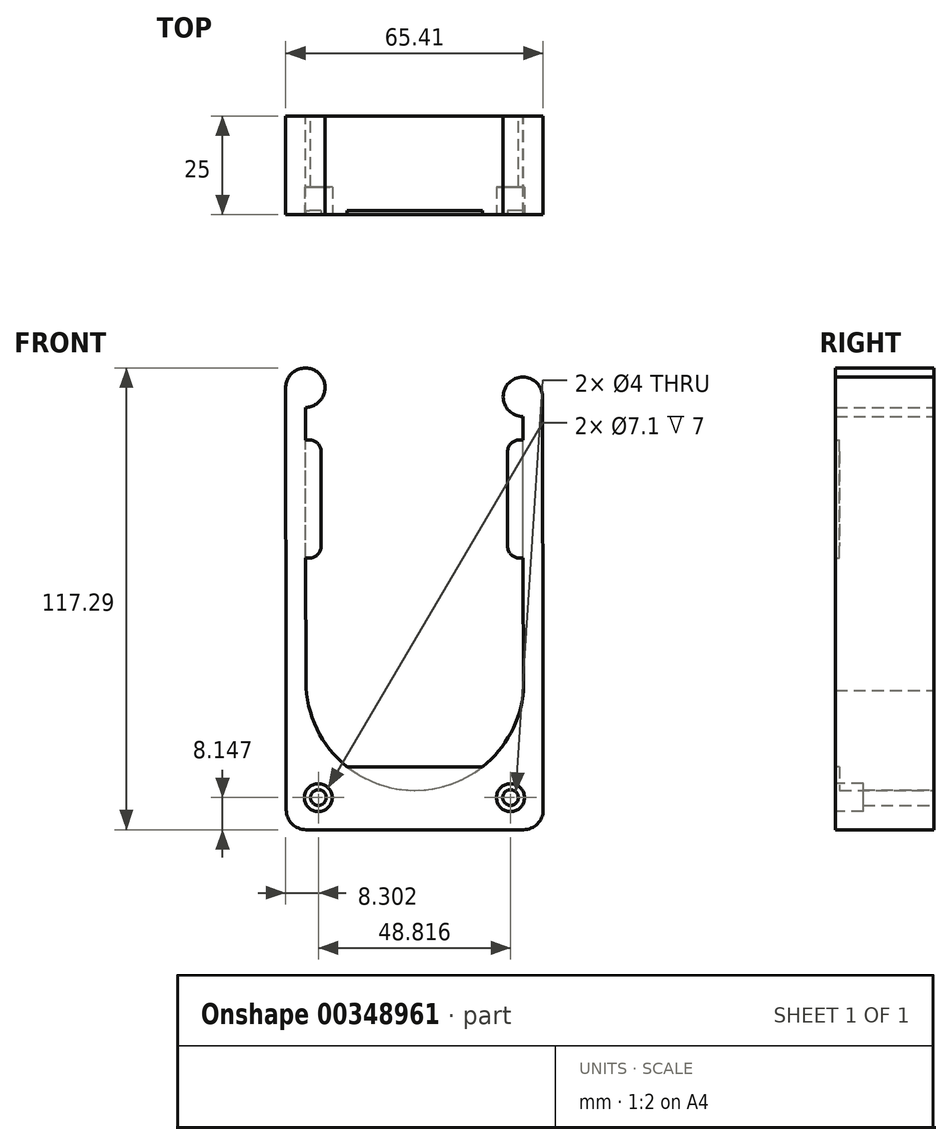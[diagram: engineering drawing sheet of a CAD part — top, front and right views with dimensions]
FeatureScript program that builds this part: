
annotation { "Feature Type Name" : "Feature", "Feature Type Description" : "" }
export const myFeature = defineFeature(function(context is Context, id is Id, definition is map)
    precondition{}
    {
        {
            var Q0;
            Q0=qCreatedBy(makeId("Front.planeOp"),FACE);
            var sketch = newSketch(context, id + "F0", { "sketchPlane" : qUnion([Q0])});
            skLineSegment(sketch, "E0.left", {"start": v(27.7, -35.98) * mm, "end": v(27.56, 33.69) * mm});
            skLineSegment(sketch, "E0.right", {"start": v(-27.56, -33.69) * mm, "end": v(-27.7, 35.98) * mm});
            skPoint(sketch, "E0.middle", {"position": v(0, 0) * mm});
            skArc(sketch, "E1", {"start": v(-27.56, -33.69) * mm, "mid": v(-1.03, -61.3) * mm, "end": v(27.7, -35.98) * mm});
            skLineSegment(sketch, "E2.1", {"start": v(32.7, -35.94) * mm, "end": v(32.55, 38.7) * mm});
            skLineSegment(sketch, "E2.3", {"start": v(-32.56, -36.07) * mm, "end": v(-32.71, 40.93) * mm});
            skArc(sketch, "E3", {"start": v(32.55, 38.7) * mm, "mid": v(24.01, 42.21) * mm, "end": v(27.56, 33.69) * mm});
            skArc(sketch, "E4", {"start": v(-27.7, 35.98) * mm, "mid": v(-24.2, 44.54) * mm, "end": v(-32.71, 40.93) * mm});
            skLineSegment(sketch, "E5", {"start": v(-32.56, -36.07) * mm, "end": v(-32.56, -66.31) * mm});
            skLineSegment(sketch, "E6", {"start": v(-27.56, -71.31) * mm, "end": v(27.7, -71.31) * mm});
            skLineSegment(sketch, "E7", {"start": v(32.7, -66.31) * mm, "end": v(32.7, -35.94) * mm});
            skLineSegment(sketch, "E8", {"start": v(0, 0) * mm, "end": v(0, -61.31) * mm, "construction": true});
            skPoint(sketch, "E9.visualSharp", {"position": v(-32.56, -71.31) * mm});
            skArc(sketch, "E9.filletArc", {"start": v(-32.56, -66.31) * mm, "mid": v(-31.1, -69.85) * mm, "end": v(-27.56, -71.31) * mm});
            skPoint(sketch, "E10.visualSharp", {"position": v(32.7, -71.31) * mm});
            skArc(sketch, "E10.filletArc", {"start": v(27.7, -71.31) * mm, "mid": v(31.24, -69.85) * mm, "end": v(32.7, -66.31) * mm});
            skCircle(sketch, "E11", {"center": v(-24.4, -63.16) * mm, "radius": 2 * mm});
            skLineSegment(sketch, "E12", {"start": v(-16.8, -55.55) * mm, "end": v(-31.1, -69.85) * mm, "construction": true});
            skCircle(sketch, "E13.MirrorC", {"center": v(24.4, -63.16) * mm, "radius": 2 * mm});
            skSolve(sketch);
        }
        {
            var Q0;
            Q0 = qSketchRegion(id + "F0", true);
            extrude(context, id + "F1", {"entities" : qUnion([Q0]), "depth" : 25 * mm});
        }
        {
            var Q0;
            Q0=makeQuery(id+"F1.opExtrude","CAP_FACE",FACE,{"disambiguationData":[OSD([sQuery(id+"F0.wireOp",EDGE,"E0.left"),sQuery(id+"F0.wireOp",EDGE,"E0.right"),sQuery(id+"F0.wireOp",EDGE,"E1"),sQuery(id+"F0.wireOp",EDGE,"E2.1"),sQuery(id+"F0.wireOp",EDGE,"E2.3"),sQuery(id+"F0.wireOp",EDGE,"E3"),sQuery(id+"F0.wireOp",EDGE,"E4"),sQuery(id+"F0.wireOp",EDGE,"E5"),sQuery(id+"F0.wireOp",EDGE,"E6"),sQuery(id+"F0.wireOp",EDGE,"E7"),sQuery(id+"F0.wireOp",EDGE,"E9.filletArc"),sQuery(id+"F0.wireOp",EDGE,"E10.filletArc"),sQuery(id+"F0.wireOp",EDGE,"E11"),sQuery(id+"F0.wireOp",EDGE,"E13.MirrorC")])],"isStart":false});
            var sketch = newSketch(context, id + "F2", { "sketchPlane" : qUnion([Q0])});
            skLineSegment(sketch, "E14.bottom", {"start": v(-27.68, 27.71) * mm, "end": v(-26.68, 27.71) * mm});
            skLineSegment(sketch, "E14.top", {"start": v(-27.68, -2.29) * mm, "end": v(-26.68, -2.29) * mm});
            skLineSegment(sketch, "E14.left", {"start": v(-27.68, 27.71) * mm, "end": v(-27.68, -2.29) * mm});
            skLineSegment(sketch, "E14.right", {"start": v(-23.68, 24.71) * mm, "end": v(-23.68, 0.71) * mm});
            skPoint(sketch, "E15.visualSharp", {"position": v(-23.68, 27.71) * mm});
            skArc(sketch, "E15.filletArc", {"start": v(-23.68, 24.71) * mm, "mid": v(-24.56, 26.83) * mm, "end": v(-26.68, 27.71) * mm});
            skPoint(sketch, "E16.visualSharp", {"position": v(-23.68, -2.29) * mm});
            skArc(sketch, "E16.filletArc", {"start": v(-26.68, -2.29) * mm, "mid": v(-24.56, -1.41) * mm, "end": v(-23.68, 0.71) * mm});
            skLineSegment(sketch, "E17.MirrorCS", {"start": v(27.68, -2.29) * mm, "end": v(26.68, -2.29) * mm});
            skLineSegment(sketch, "E18.MirrorCS", {"start": v(27.68, 27.71) * mm, "end": v(26.68, 27.71) * mm});
            skArc(sketch, "E19.MirrorCS", {"start": v(26.68, -2.29) * mm, "mid": v(24.56, -1.41) * mm, "end": v(23.68, 0.71) * mm});
            skArc(sketch, "E20.MirrorCS", {"start": v(23.68, 24.71) * mm, "mid": v(24.56, 26.83) * mm, "end": v(26.68, 27.71) * mm});
            skLineSegment(sketch, "E21.MirrorCS", {"start": v(23.68, 24.71) * mm, "end": v(23.68, 0.71) * mm});
            skLineSegment(sketch, "E22.MirrorCS", {"start": v(27.68, 27.71) * mm, "end": v(27.68, -2.29) * mm});
            skPoint(sketch, "E23.MirrorP", {"position": v(23.68, -2.29) * mm});
            skPoint(sketch, "E24.MirrorP", {"position": v(23.68, 27.71) * mm});
            skLineSegment(sketch, "E25", {"start": v(-17.1, -55.31) * mm, "end": v(17.33, -55.31) * mm});
            skArc(sketch, "E26", {"start": v(-17.1, -55.31) * mm, "mid": v(0.12, -61.31) * mm, "end": v(17.33, -55.31) * mm});
            skLineSegment(sketch, "E27", {"start": v(0.12, -55.31) * mm, "end": v(0.12, -61.31) * mm});
            skSolve(sketch);
        }
        {
            var Q0;
            Q0 = qSketchRegion(id + "F2", true);
            extrude(context, id + "F3", {"entities" : qUnion([Q0]), "operationType" : NewBodyOperationType.ADD, "oppositeDirection" : true, "depth" : 1 * mm});
        }
        {
            var Q0;
            Q0=makeQuery(id+"F3.boolean.opBoolean","MERGE",FACE,{"derivedFrom":[makeQuery(id+"F1.opExtrude","CAP_FACE",FACE,{"disambiguationData":[OSD([sQuery(id+"F0.wireOp",EDGE,"E0.left"),sQuery(id+"F0.wireOp",EDGE,"E0.right"),sQuery(id+"F0.wireOp",EDGE,"E1"),sQuery(id+"F0.wireOp",EDGE,"E2.1"),sQuery(id+"F0.wireOp",EDGE,"E2.3"),sQuery(id+"F0.wireOp",EDGE,"E3"),sQuery(id+"F0.wireOp",EDGE,"E4"),sQuery(id+"F0.wireOp",EDGE,"E5"),sQuery(id+"F0.wireOp",EDGE,"E6"),sQuery(id+"F0.wireOp",EDGE,"E7"),sQuery(id+"F0.wireOp",EDGE,"E9.filletArc"),sQuery(id+"F0.wireOp",EDGE,"E10.filletArc"),sQuery(id+"F0.wireOp",EDGE,"E11"),sQuery(id+"F0.wireOp",EDGE,"E13.MirrorC")])],"isStart":false}),makeQuery(id+"F3.opExtrude","CAP_FACE",FACE,{"disambiguationData":[OSD([sQuery(id+"F2.wireOp",EDGE,"E14.bottom"),sQuery(id+"F2.wireOp",EDGE,"E14.top"),sQuery(id+"F2.wireOp",EDGE,"E14.left"),sQuery(id+"F2.wireOp",EDGE,"E14.right"),sQuery(id+"F2.wireOp",EDGE,"E15.filletArc"),sQuery(id+"F2.wireOp",EDGE,"E16.filletArc")])],"isStart":true}),makeQuery(id+"F3.opExtrude","CAP_FACE",FACE,{"disambiguationData":[OSD([sQuery(id+"F2.wireOp",EDGE,"E17.MirrorCS"),sQuery(id+"F2.wireOp",EDGE,"E18.MirrorCS"),sQuery(id+"F2.wireOp",EDGE,"E19.MirrorCS"),sQuery(id+"F2.wireOp",EDGE,"E20.MirrorCS"),sQuery(id+"F2.wireOp",EDGE,"E21.MirrorCS"),sQuery(id+"F2.wireOp",EDGE,"E22.MirrorCS")])],"isStart":true}),makeQuery(id+"F3.opExtrude","CAP_FACE",FACE,{"disambiguationData":[OSD([sQuery(id+"F2.wireOp",EDGE,"E25"),sQuery(id+"F2.wireOp",EDGE,"E26")])],"isStart":true})]});
            var sketch = newSketch(context, id + "F4", { "sketchPlane" : qUnion([Q0])});
            skCircle(sketch, "E28", {"center": v(-24.4, -63.16) * mm, "radius": 3.55 * mm});
            skCircle(sketch, "E29", {"center": v(24.4, -63.16) * mm, "radius": 3.55 * mm});
            skSolve(sketch);
        }
        {
            var Q0;
            Q0 = qSketchRegion(id + "F4", true);
            extrude(context, id + "F5", {"entities" : qUnion([Q0]), "operationType" : NewBodyOperationType.REMOVE, "oppositeDirection" : true, "depth" : 7 * mm});
        }
    });
